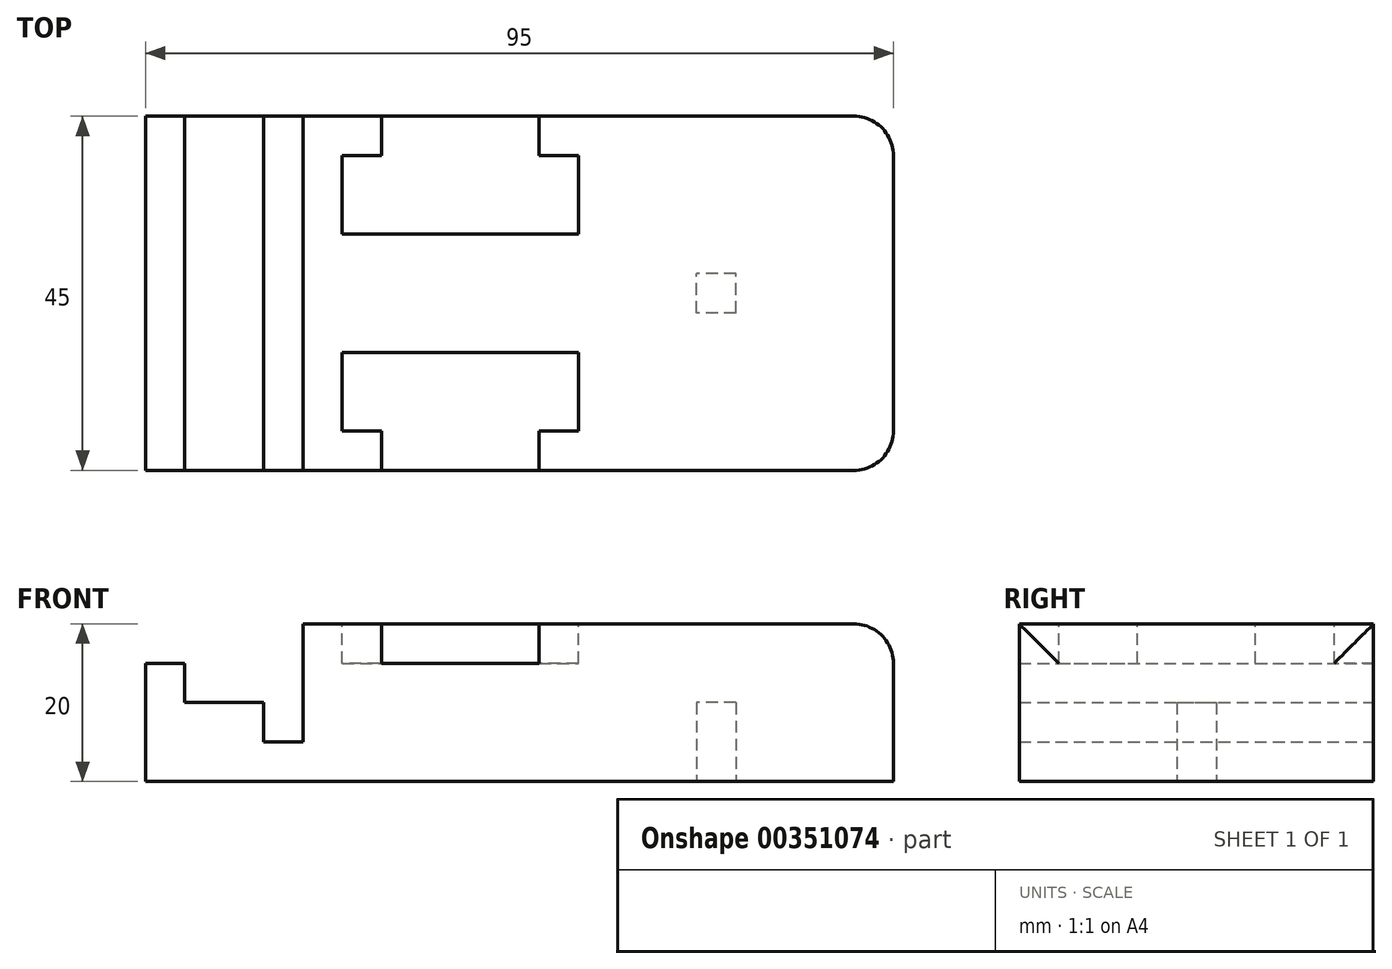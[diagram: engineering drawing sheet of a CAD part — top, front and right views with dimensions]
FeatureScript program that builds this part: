
annotation { "Feature Type Name" : "Feature", "Feature Type Description" : "" }
export const myFeature = defineFeature(function(context is Context, id is Id, definition is map)
    precondition{}
    {
        {
            var Q0;
            Q0=qCreatedBy(makeId("Top.planeOp"),FACE);
            var sketch = newSketch(context, id + "F0", { "sketchPlane" : qUnion([Q0])});
            skLineSegment(sketch, "E0.bottom", {"start": v(47.5, 22.5) * mm, "end": v(-47.5, 22.5) * mm});
            skLineSegment(sketch, "E0.top", {"start": v(47.5, -22.5) * mm, "end": v(-47.5, -22.5) * mm});
            skLineSegment(sketch, "E0.left", {"start": v(47.5, 22.5) * mm, "end": v(47.5, -22.5) * mm});
            skLineSegment(sketch, "E0.right", {"start": v(-47.5, 22.5) * mm, "end": v(-47.5, -22.5) * mm});
            skPoint(sketch, "E0.middle", {"position": v(0, 0) * mm});
            skLineSegment(sketch, "E1", {"start": v(-47.5, 0) * mm, "end": v(-42.5, 0) * mm, "construction": true});
            skLineSegment(sketch, "E2", {"start": v(-42.5, -22.5) * mm, "end": v(-42.5, 22.5) * mm});
            skLineSegment(sketch, "E3", {"start": v(-42.5, 0) * mm, "end": v(-32.5, 0) * mm, "construction": true});
            skLineSegment(sketch, "E4", {"start": v(-32.5, -22.5) * mm, "end": v(-32.5, 22.5) * mm});
            skLineSegment(sketch, "E5", {"start": v(-32.5, 0) * mm, "end": v(-27.5, 0) * mm, "construction": true});
            skLineSegment(sketch, "E6", {"start": v(-27.5, -22.5) * mm, "end": v(-27.5, 22.5) * mm});
            skLineSegment(sketch, "E7", {"start": v(47.5, 0) * mm, "end": v(27.5, 0) * mm});
            skLineSegment(sketch, "E8", {"start": v(27.5, 0) * mm, "end": v(27.5, 2.5) * mm});
            skLineSegment(sketch, "E9", {"start": v(27.5, -2.5) * mm, "end": v(27.5, 0) * mm});
            skLineSegment(sketch, "E10", {"start": v(25, 0) * mm, "end": v(27.5, 0) * mm, "construction": true});
            skPoint(sketch, "E11", {"position": v(25, 0) * mm});
            skLineSegment(sketch, "E12", {"start": v(0, 0) * mm, "end": v(25, 0) * mm, "construction": true});
            skSolve(sketch);
        }
        {
            var Q0;
            {var subQ0=sQuery(id+"F0.wireOp",EDGE,"E0.right");Q0=makeQuery(id+"F0.imprint","IMPRINT",FACE,{"disambiguationData":[TD([[makeQuery(id+"F0.imprint","IMPRINT",EDGE,{"derivedFrom":subQ0}),1.0]])]});}
            extrude(context, id + "F1", {"entities" : qUnion([Q0]), "depth" : 15 * mm});
        }
        {
            var Q0;
            {var subQ0=sQuery(id+"F0.wireOp",EDGE,"E2");Q0=makeQuery(id+"F0.imprint","IMPRINT",FACE,{"disambiguationData":[TD([[makeQuery(id+"F0.imprint","IMPRINT",EDGE,{"derivedFrom":subQ0}),-1.0]])]});}
            extrude(context, id + "F2", {"entities" : qUnion([Q0]), "operationType" : NewBodyOperationType.ADD, "depth" : 10 * mm});
        }
        {
            var Q0;
            {var subQ0=sQuery(id+"F0.wireOp",EDGE,"E4");Q0=makeQuery(id+"F0.imprint","IMPRINT",FACE,{"disambiguationData":[TD([[makeQuery(id+"F0.imprint","IMPRINT",EDGE,{"derivedFrom":subQ0}),-1.0]])]});}
            extrude(context, id + "F3", {"entities" : qUnion([Q0]), "operationType" : NewBodyOperationType.ADD, "depth" : 5 * mm});
        }
        {
            var Q0;
            {var subQ0=sQuery(id+"F0.wireOp",EDGE,"E0.left");Q0=makeQuery(id+"F0.imprint","IMPRINT",FACE,{"disambiguationData":[TD([[makeQuery(id+"F0.imprint","IMPRINT",EDGE,{"derivedFrom":subQ0}),-1.0]])]});}
            extrude(context, id + "F4", {"entities" : qUnion([Q0]), "operationType" : NewBodyOperationType.ADD, "depth" : 20 * mm});
        }
        {
            var Q0;
            Q0=makeQuery(id+"F4.opExtrude","CAP_FACE",FACE,{"disambiguationData":[OSD([sQuery(id+"F0.wireOp",EDGE,"E0.bottom"),sQuery(id+"F0.wireOp",EDGE,"E0.top"),sQuery(id+"F0.wireOp",EDGE,"E0.left"),sQuery(id+"F0.wireOp",EDGE,"E6")])],"isStart":false});
            var sketch = newSketch(context, id + "F5", { "sketchPlane" : qUnion([Q0])});
            skLineSegment(sketch, "E13", {"start": v(-27.5, 0) * mm, "end": v(-22.5, 0) * mm, "construction": true});
            skPoint(sketch, "E13.endSnap0", {"position": v(-27.5, 0) * mm});
            skLineSegment(sketch, "E14", {"start": v(-22.5, 0) * mm, "end": v(-22.5, 22.5) * mm, "construction": true});
            skLineSegment(sketch, "E15", {"start": v(-22.5, 22.5) * mm, "end": v(-22.5, -22.5) * mm, "construction": true});
            skLineSegment(sketch, "E16", {"start": v(-22.5, -22.5) * mm, "end": v(-17.5, -22.5) * mm, "construction": true});
            skLineSegment(sketch, "E17", {"start": v(-17.5, -22.5) * mm, "end": v(-17.5, 22.5) * mm, "construction": true});
            skLineSegment(sketch, "E18", {"start": v(-17.5, 22.5) * mm, "end": v(2.5, 22.5) * mm, "construction": true});
            skLineSegment(sketch, "E19", {"start": v(2.5, 22.5) * mm, "end": v(2.5, -22.5) * mm, "construction": true});
            skLineSegment(sketch, "E20", {"start": v(2.5, -22.5) * mm, "end": v(7.5, -22.5) * mm, "construction": true});
            skLineSegment(sketch, "E21", {"start": v(7.5, -22.5) * mm, "end": v(7.5, 22.5) * mm, "construction": true});
            skLineSegment(sketch, "E22", {"start": v(2.5, 22.5) * mm, "end": v(2.5, 17.5) * mm});
            skLineSegment(sketch, "E23", {"start": v(2.5, 17.5) * mm, "end": v(7.5, 17.5) * mm});
            skLineSegment(sketch, "E24", {"start": v(7.5, 17.5) * mm, "end": v(7.5, 7.5) * mm});
            skLineSegment(sketch, "E25", {"start": v(7.5, 7.5) * mm, "end": v(-22.5, 7.5) * mm});
            skLineSegment(sketch, "E26", {"start": v(-22.5, 7.5) * mm, "end": v(-22.5, 17.5) * mm});
            skPoint(sketch, "E26.endSnap0", {"position": v(5, 17.5) * mm});
            skLineSegment(sketch, "E27", {"start": v(-22.5, 17.5) * mm, "end": v(-17.5, 17.5) * mm});
            skLineSegment(sketch, "E28", {"start": v(-17.5, 17.5) * mm, "end": v(-17.5, 22.5) * mm});
            skLineSegment(sketch, "E29", {"start": v(2.5, -22.5) * mm, "end": v(2.5, -17.5) * mm});
            skLineSegment(sketch, "E30", {"start": v(2.5, -17.5) * mm, "end": v(7.5, -17.5) * mm});
            skLineSegment(sketch, "E31", {"start": v(7.5, -17.5) * mm, "end": v(7.5, -7.5) * mm});
            skLineSegment(sketch, "E32", {"start": v(7.5, -7.5) * mm, "end": v(-22.5, -7.5) * mm});
            skLineSegment(sketch, "E33", {"start": v(-22.5, -7.5) * mm, "end": v(-22.5, -12.5) * mm});
            skLineSegment(sketch, "E34", {"start": v(-22.5, -12.5) * mm, "end": v(-22.5, -17.5) * mm});
            skLineSegment(sketch, "E35", {"start": v(-22.5, -17.5) * mm, "end": v(-17.5, -17.5) * mm});
            skLineSegment(sketch, "E36", {"start": v(-17.5, -17.5) * mm, "end": v(-17.5, -22.5) * mm});
            skSolve(sketch);
        }
        {
            var Q0;
            {var subQ0=sQuery(id+"F5.wireOp",EDGE,"E29");Q0=makeQuery(id+"F5.imprint","IMPRINT",FACE,{"disambiguationData":[TD([[makeQuery(id+"F5.imprint","IMPRINT",EDGE,{"derivedFrom":subQ0}),1.0]])]});}
            var Q1;
            {var subQ0=sQuery(id+"F5.wireOp",EDGE,"E22");Q1=makeQuery(id+"F5.imprint","IMPRINT",FACE,{"disambiguationData":[TD([[makeQuery(id+"F5.imprint","IMPRINT",EDGE,{"derivedFrom":subQ0}),-1.0]])]});}
            extrude(context, id + "F6", {"entities" : qUnion([Q0, Q1]), "operationType" : NewBodyOperationType.REMOVE, "oppositeDirection" : true, "depth" : 5 * mm});
        }
        {
            var Q0;
            {var subQ6=sQuery(id+"F0.wireOp",EDGE,"E6");Q0=makeQuery(id+"F0.imprint","IMPRINT",FACE,{"disambiguationData":[TD([[makeQuery(id+"F0.imprint","IMPRINT",EDGE,{"derivedFrom":subQ6}),-1.0]])]});}
            var sketch = newSketch(context, id + "F7", { "sketchPlane" : qUnion([Q0])});
            skLineSegment(sketch, "E37", {"start": v(0, 0) * mm, "end": v(25, 0) * mm, "construction": true});
            skLineSegment(sketch, "E38.bottom", {"start": v(27.5, -2.5) * mm, "end": v(22.5, -2.5) * mm});
            skLineSegment(sketch, "E38.top", {"start": v(27.5, 2.5) * mm, "end": v(22.5, 2.5) * mm});
            skLineSegment(sketch, "E38.left", {"start": v(27.5, -2.5) * mm, "end": v(27.5, 2.5) * mm});
            skLineSegment(sketch, "E38.right", {"start": v(22.5, -2.5) * mm, "end": v(22.5, 2.5) * mm});
            skPoint(sketch, "E38.middle", {"position": v(25, 0) * mm});
            skSolve(sketch);
        }
        {
            var Q0;
            Q0=makeQuery(id+"F7.imprint","IMPRINT",FACE,{"disambiguationData":[TD([[makeQuery(id+"F7.imprint","IMPRINT",EDGE,{"derivedFrom":sQuery(id+"F7.wireOp",EDGE,"E38.bottom")}),-1.0]])]});
            extrude(context, id + "F8", {"entities" : qUnion([Q0]), "operationType" : NewBodyOperationType.REMOVE, "oppositeDirection" : true, "depth" : -10 * mm});
        }
        {
            var Q0;
            Q0=makeQuery(id+"F4.opExtrude","CAP_EDGE",EDGE,{"disambiguationData":[OSD([sQuery(id+"F0.wireOp",EDGE,"E0.left")])],"isStart":false});
            var Q1;
            Q1=makeQuery(id+"F4.opExtrude","SWEPT_EDGE",EDGE,{"disambiguationData":[OSD([sQuery(id+"F0.wireOp",EDGE,"E0.bottom"),sQuery(id+"F0.wireOp",EDGE,"E0.left")])]});
            var Q2;
            Q2=makeQuery(id+"F4.opExtrude","SWEPT_EDGE",EDGE,{"disambiguationData":[OSD([sQuery(id+"F0.wireOp",EDGE,"E0.top"),sQuery(id+"F0.wireOp",EDGE,"E0.left")])]});
            fillet(context, id + "F9", {"entities" : qUnion([Q0, Q1, Q2]), "radius" : 5 * mm, "tangentPropagation" : true, "allowEdgeOverflow" : false});
        }
    });
